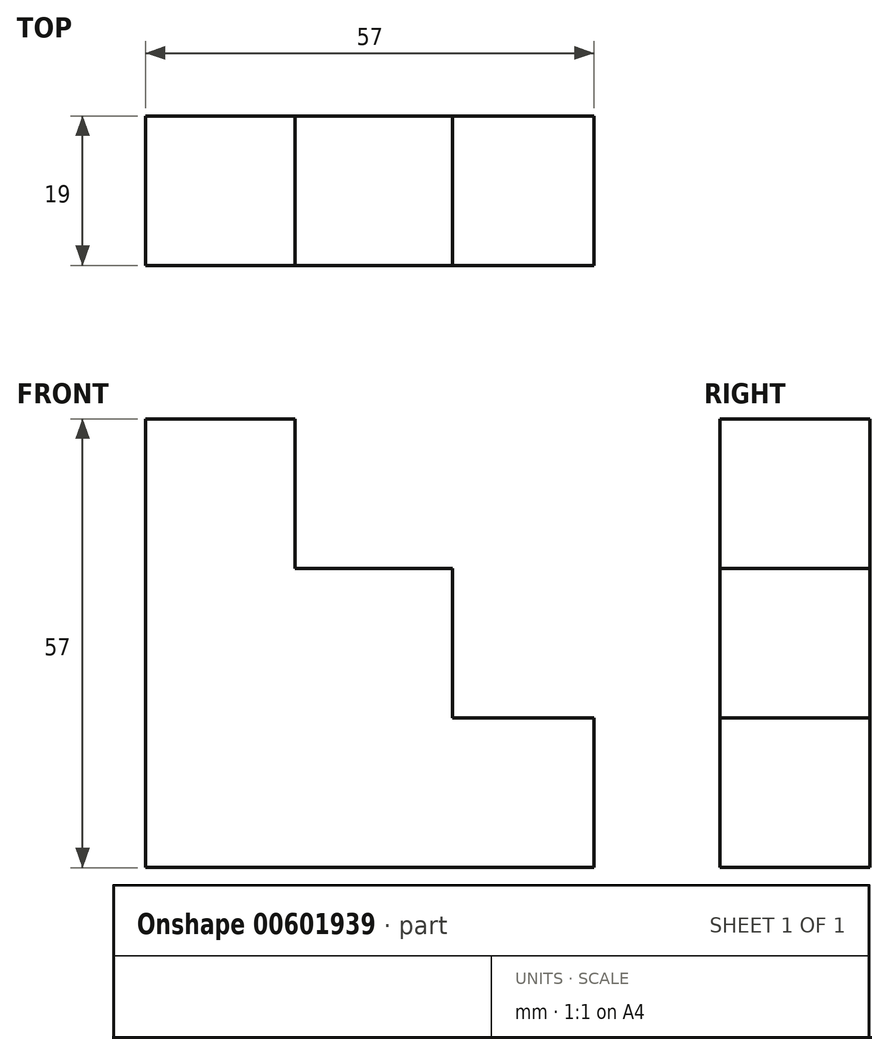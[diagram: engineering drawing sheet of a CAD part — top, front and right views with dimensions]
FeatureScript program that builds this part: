
annotation { "Feature Type Name" : "Feature", "Feature Type Description" : "" }
export const myFeature = defineFeature(function(context is Context, id is Id, definition is map)
    precondition{}
    {
        {
            var Q0;
            Q0=qCreatedBy(makeId("Front.planeOp"),FACE);
            var sketch = newSketch(context, id + "F0", { "sketchPlane" : qUnion([Q0])});
            skLineSegment(sketch, "E0", {"start": v(-32.77, -12.6) * mm, "end": v(-32.77, -31.6) * mm});
            skLineSegment(sketch, "E1", {"start": v(-32.77, -12.6) * mm, "end": v(24.23, -12.6) * mm});
            skLineSegment(sketch, "E2", {"start": v(24.23, -31.6) * mm, "end": v(-32.77, -31.6) * mm});
            skLineSegment(sketch, "E3", {"start": v(24.23, -12.6) * mm, "end": v(24.23, -31.6) * mm});
            skLineSegment(sketch, "E4", {"start": v(-32.77, -12.6) * mm, "end": v(-32.77, 6.4) * mm});
            skLineSegment(sketch, "E5", {"start": v(-32.77, 6.4) * mm, "end": v(6.23, 6.4) * mm});
            skLineSegment(sketch, "E6", {"start": v(6.23, 6.4) * mm, "end": v(6.23, -12.6) * mm});
            skLineSegment(sketch, "E7", {"start": v(-32.77, 6.4) * mm, "end": v(-32.77, 25.4) * mm});
            skLineSegment(sketch, "E8", {"start": v(-32.77, 25.4) * mm, "end": v(-13.77, 25.4) * mm});
            skLineSegment(sketch, "E9", {"start": v(-13.77, 25.4) * mm, "end": v(-13.77, 6.4) * mm});
            skSolve(sketch);
        }
        {
            var Q0;
            Q0 = qSketchRegion(id + "F0", true);
            extrude(context, id + "F1", {"entities" : qUnion([Q0]), "depth" : 19 * mm, "offsetDistance" : 25.4 * mm});
        }
    });
